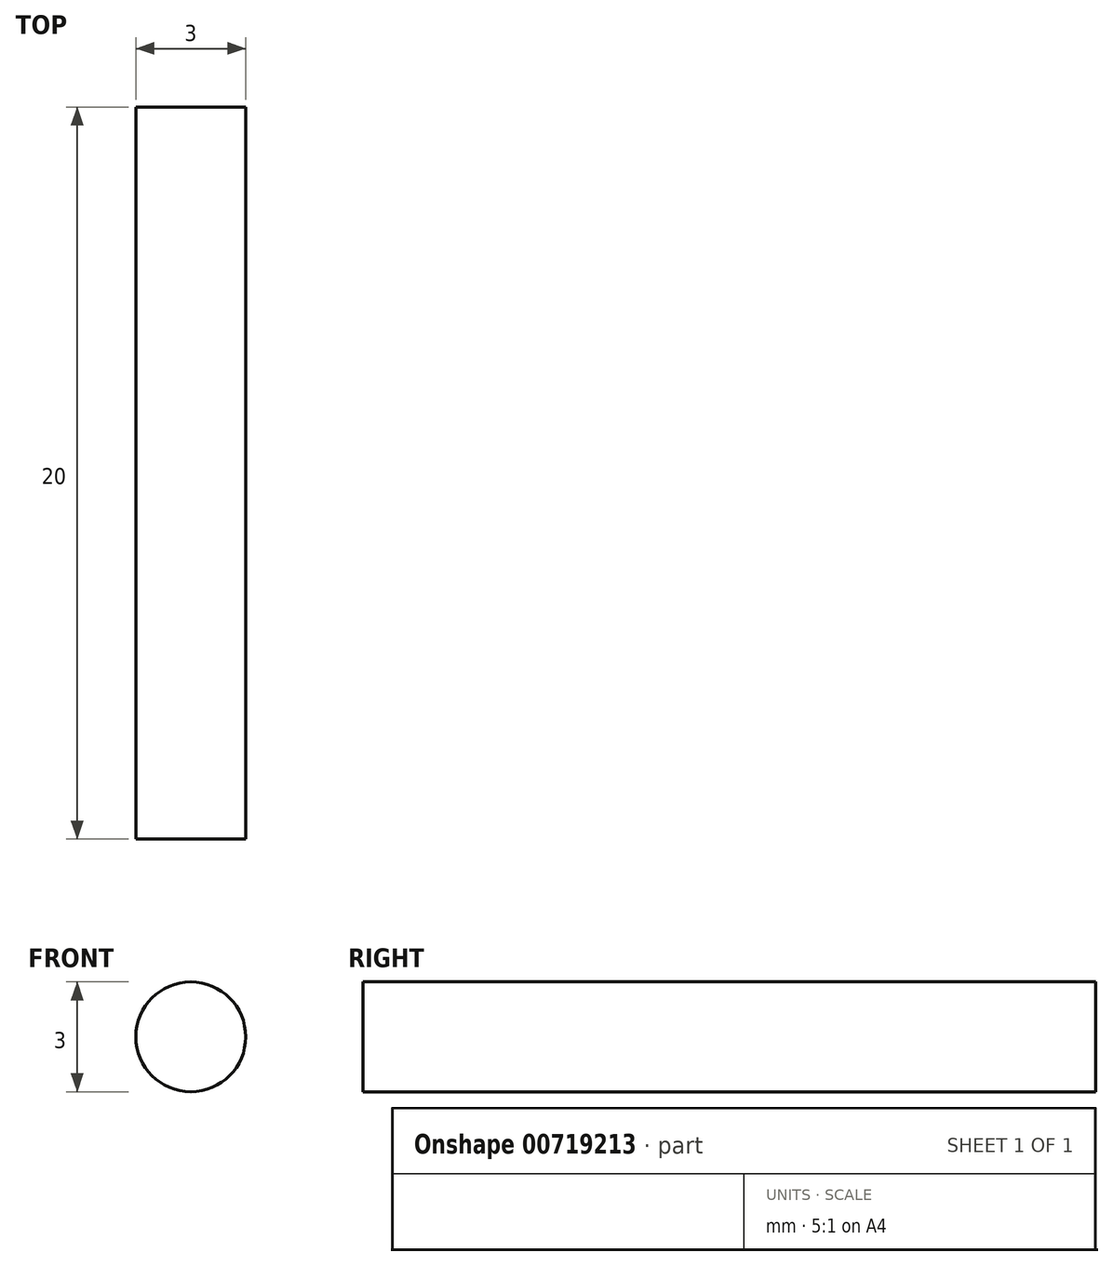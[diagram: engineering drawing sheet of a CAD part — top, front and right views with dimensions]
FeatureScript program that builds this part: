
annotation { "Feature Type Name" : "Feature", "Feature Type Description" : "" }
export const myFeature = defineFeature(function(context is Context, id is Id, definition is map)
    precondition{}
    {
        {
            var Q0;
            Q0=qCreatedBy(makeId("Front.planeOp"),FACE);
            var sketch = newSketch(context, id + "F0", { "sketchPlane" : qUnion([Q0])});
            skCircle(sketch, "E0", {"center": v(0, 0) * mm, "radius": 1.5 * mm});
            skSolve(sketch);
        }
        {
            var Q0;
            Q0 = qSketchRegion(id + "F0", true);
            extrude(context, id + "F1", {"entities" : qUnion([Q0]), "depth" : 20 * mm, "offsetDistance" : 25 * mm});
        }
    });
